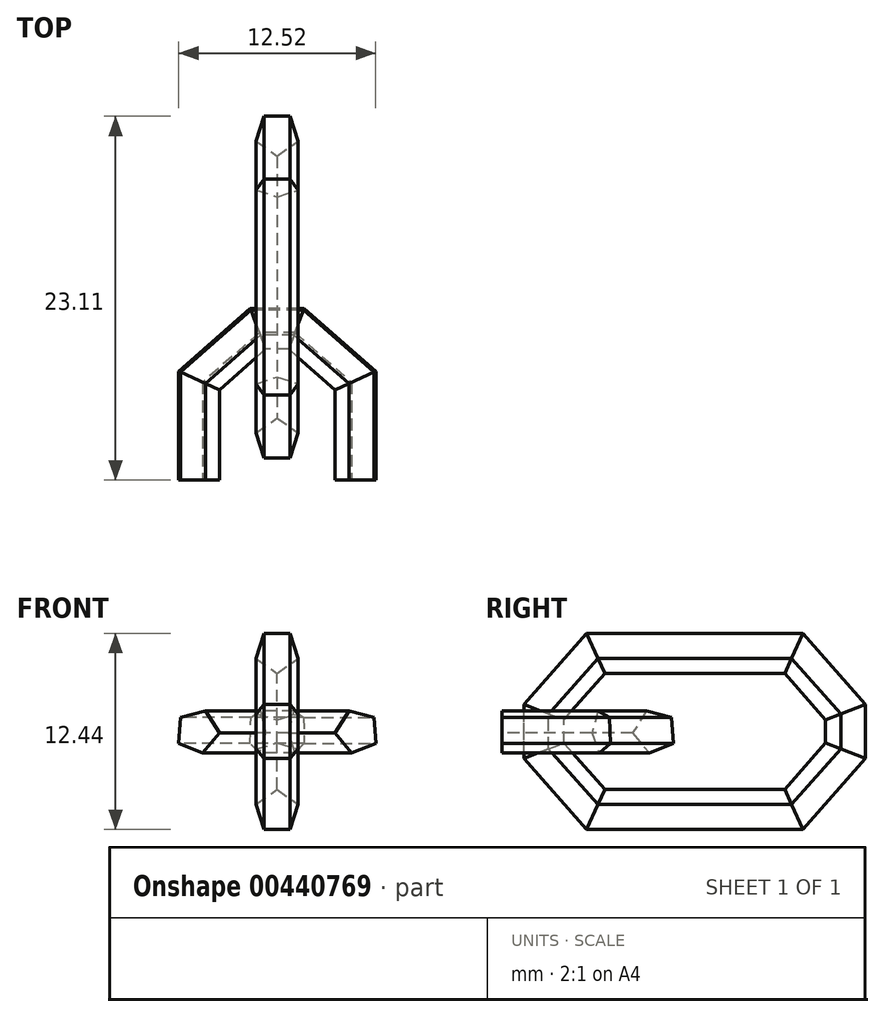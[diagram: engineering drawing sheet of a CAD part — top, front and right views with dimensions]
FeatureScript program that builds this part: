
annotation { "Feature Type Name" : "Feature", "Feature Type Description" : "" }
export const myFeature = defineFeature(function(context is Context, id is Id, definition is map)
    precondition{}
    {
        {
            var Q0;
            Q0=qCreatedBy(makeId("Front.planeOp"),FACE);
            var sketch = newSketch(context, id + "F0", { "sketchPlane" : qUnion([Q0])});
            skCircle(sketch, "E0.cCircle", {"center": v(0, 0) * mm, "radius": 1.14 * mm, "construction": true});
            skLineSegment(sketch, "E0.0", {"start": v(-1.34, 0.43) * mm, "end": v(0, 1.4) * mm});
            skLineSegment(sketch, "E0.1", {"start": v(0, 1.4) * mm, "end": v(1.34, 0.43) * mm});
            skLineSegment(sketch, "E0.2", {"start": v(1.34, 0.43) * mm, "end": v(0.83, -1.14) * mm});
            skLineSegment(sketch, "E0.3", {"start": v(0.83, -1.14) * mm, "end": v(-0.83, -1.14) * mm});
            skLineSegment(sketch, "E0.4", {"start": v(-0.83, -1.14) * mm, "end": v(-1.34, 0.43) * mm});
            skPoint(sketch, "E0.0.midPoint", {"position": v(-0.67, 0.92) * mm});
            skSolve(sketch);
        }
        {
            var Q0;
            Q0=qCreatedBy(makeId("Right.planeOp"),FACE);
            var sketch = newSketch(context, id + "F1", { "sketchPlane" : qUnion([Q0])});
            skPoint(sketch, "E1", {"position": v(-6.35, 0) * mm});
            skPoint(sketch, "E2", {"position": v(-9.72, 3.8) * mm});
            skPoint(sketch, "E3", {"position": v(-9.72, 6.35) * mm});
            skPoint(sketch, "E4", {"position": v(-6.35, 10.16) * mm});
            skPoint(sketch, "E5", {"position": v(6.35, 10.16) * mm});
            skPoint(sketch, "E6", {"position": v(9.72, 6.35) * mm});
            skPoint(sketch, "E7", {"position": v(9.72, 3.8) * mm});
            skPoint(sketch, "E8", {"position": v(6.35, 0) * mm});
            skLineSegment(sketch, "E9", {"start": v(-9.72, 6.35) * mm, "end": v(-9.72, 3.8) * mm});
            skLineSegment(sketch, "E10", {"start": v(-9.72, 3.8) * mm, "end": v(-6.35, 0) * mm});
            skLineSegment(sketch, "E11", {"start": v(-6.35, 0) * mm, "end": v(6.35, 0) * mm});
            skLineSegment(sketch, "E12", {"start": v(6.35, 0) * mm, "end": v(9.72, 3.8) * mm});
            skLineSegment(sketch, "E13", {"start": v(9.72, 3.8) * mm, "end": v(9.72, 6.35) * mm});
            skLineSegment(sketch, "E14", {"start": v(9.72, 6.35) * mm, "end": v(6.35, 10.16) * mm});
            skLineSegment(sketch, "E15", {"start": v(6.35, 10.16) * mm, "end": v(-6.35, 10.16) * mm});
            skLineSegment(sketch, "E16", {"start": v(-6.35, 10.16) * mm, "end": v(-9.72, 6.35) * mm});
            skSolve(sketch);
        }
        {
            var Q0;
            Q0=makeQuery(id+"F0.imprint","IMPRINT",FACE,{"disambiguationData":[TD([[makeQuery(id+"F0.imprint","IMPRINT",EDGE,{"derivedFrom":sQuery(id+"F0.wireOp",EDGE,"E0.0")}),-1.0]])]});
            var Q1;
            Q1 = qConstructionFilter(qBodyType(qCreatedBy(id + "F1" ,EDGE), BodyType.WIRE), ConstructionObject.NO);
            sweep(context, id + "F2", {"profiles" : qUnion([Q0]), "path" : qUnion([Q1])});
        }
        {
            var Q0;
            Q0=qCreatedBy(makeId("Top.planeOp"),FACE);
            cPlane(context, id + "F3", {"entities" : qUnion([Q0]), "cplaneType" : CPlaneType.OFFSET, "offset" : 5.08 * mm, "width" : 152.4 * mm, "height" : 152.4 * mm});
        }
        {
            var Q0;
            Q0=qCreatedBy(id+"F3.planeOp",FACE);
            var sketch = newSketch(context, id + "F4", { "sketchPlane" : qUnion([Q0])});
            skPoint(sketch, "E17", {"position": v(-1.27, -2.54) * mm});
            skPoint(sketch, "E18", {"position": v(-5.08, -5.9) * mm});
            skPoint(sketch, "E19", {"position": v(-5.08, -12.26) * mm});
            skPoint(sketch, "E20", {"position": v(5.08, -12.25) * mm});
            skPoint(sketch, "E21", {"position": v(5.08, -5.9) * mm});
            skPoint(sketch, "E22", {"position": v(1.27, -2.54) * mm});
            skLineSegment(sketch, "E23", {"start": v(-1.27, -2.54) * mm, "end": v(-5.08, -5.9) * mm});
            skLineSegment(sketch, "E24", {"start": v(-5.08, -5.9) * mm, "end": v(-5.08, -12.26) * mm});
            skLineSegment(sketch, "E25", {"start": v(-1.27, -2.54) * mm, "end": v(1.27, -2.54) * mm});
            skLineSegment(sketch, "E26", {"start": v(1.27, -2.54) * mm, "end": v(5.08, -5.9) * mm});
            skLineSegment(sketch, "E27", {"start": v(5.08, -12.25) * mm, "end": v(5.08, -5.9) * mm});
            skPoint(sketch, "E28", {"position": v(0, -2.54) * mm});
            skLineSegment(sketch, "E29", {"start": v(0, -2.54) * mm, "end": v(-1.27, -2.54) * mm});
            skLineSegment(sketch, "E30", {"start": v(0, -2.54) * mm, "end": v(1.27, -2.54) * mm});
            skSolve(sketch);
        }
        {
            var Q0;
            Q0=qCreatedBy(makeId("Right.planeOp"),FACE);
            var sketch = newSketch(context, id + "F5", { "sketchPlane" : qUnion([Q0])});
            skCircle(sketch, "E31.cCircle", {"center": v(-2.55, 5.08) * mm, "radius": 1.14 * mm, "construction": true});
            skLineSegment(sketch, "E31.0", {"start": v(-3.95, 4.99) * mm, "end": v(-3.07, 6.38) * mm});
            skLineSegment(sketch, "E31.1", {"start": v(-3.07, 6.38) * mm, "end": v(-1.47, 5.98) * mm});
            skLineSegment(sketch, "E31.2", {"start": v(-1.47, 5.98) * mm, "end": v(-1.36, 4.33) * mm});
            skLineSegment(sketch, "E31.3", {"start": v(-1.36, 4.33) * mm, "end": v(-2.9, 3.72) * mm});
            skLineSegment(sketch, "E31.4", {"start": v(-2.9, 3.72) * mm, "end": v(-3.95, 4.99) * mm});
            skPoint(sketch, "E31.0.midPoint", {"position": v(-3.5, 5.69) * mm});
            skSolve(sketch);
        }
        {
            var Q0;
            Q0 = qSketchRegion(id + "F5", true);
            var Q1;
            Q1=sQuery(id+"F4.wireOp",EDGE,"E29");
            var Q2;
            Q2=sQuery(id+"F4.wireOp",EDGE,"E23");
            var Q3;
            Q3=sQuery(id+"F4.wireOp",EDGE,"E24");
            sweep(context, id + "F6", {"profiles" : qUnion([Q0]), "path" : qUnion([Q1, Q2, Q3])});
        }
        {
            var Q0;
            Q0 = qSketchRegion(id + "F5", true);
            var Q1;
            Q1=sQuery(id+"F4.wireOp",EDGE,"E30");
            var Q2;
            Q2=sQuery(id+"F4.wireOp",EDGE,"E26");
            var Q3;
            Q3=sQuery(id+"F4.wireOp",EDGE,"E27");
            sweep(context, id + "F7", {"operationType" : NewBodyOperationType.ADD, "profiles" : qUnion([Q0]), "path" : qUnion([Q1, Q2, Q3])});
        }
    });
